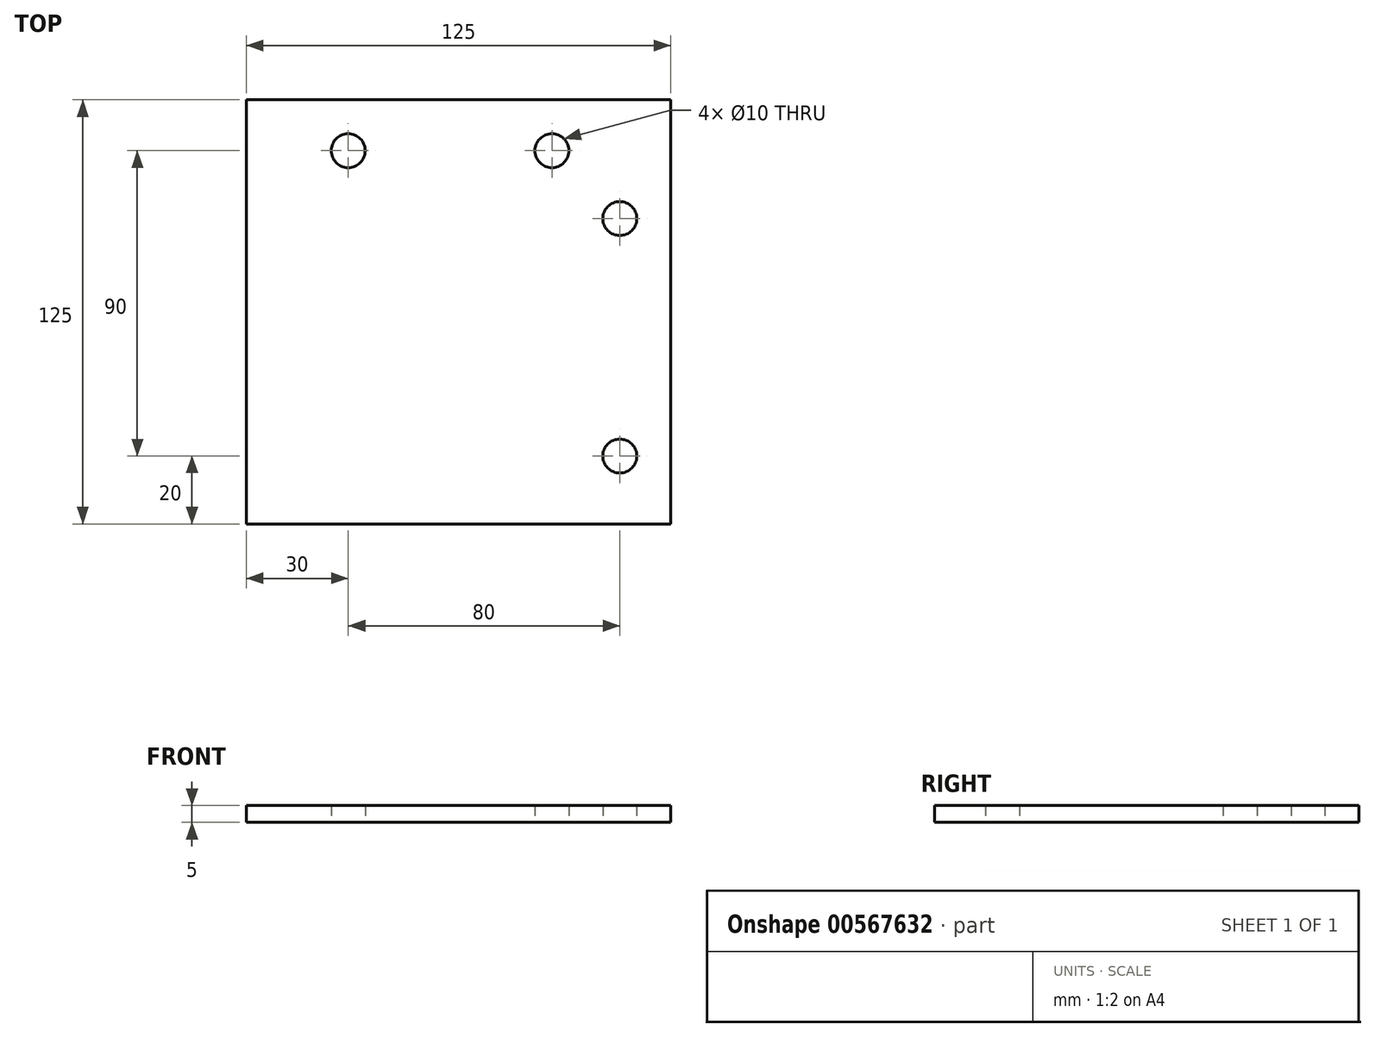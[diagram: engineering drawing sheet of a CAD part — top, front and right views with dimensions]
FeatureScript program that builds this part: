
annotation { "Feature Type Name" : "Feature", "Feature Type Description" : "" }
export const myFeature = defineFeature(function(context is Context, id is Id, definition is map)
    precondition{}
    {
        {
            var Q0;
            Q0=qCreatedBy(makeId("Top.planeOp"),FACE);
            var sketch = newSketch(context, id + "F0", { "sketchPlane" : qUnion([Q0])});
            skLineSegment(sketch, "E0.bottom", {"start": v(62.5, -62.5) * mm, "end": v(-62.5, -62.5) * mm});
            skLineSegment(sketch, "E0.top", {"start": v(62.5, 62.5) * mm, "end": v(-62.5, 62.5) * mm});
            skLineSegment(sketch, "E0.left", {"start": v(62.5, -62.5) * mm, "end": v(62.5, 62.5) * mm});
            skLineSegment(sketch, "E0.right", {"start": v(-62.5, -62.5) * mm, "end": v(-62.5, 62.5) * mm});
            skPoint(sketch, "E0.middle", {"position": v(0, 0) * mm});
            skCircle(sketch, "E1", {"center": v(27.5, 47.5) * mm, "radius": 5 * mm});
            skCircle(sketch, "E2", {"center": v(-32.5, 47.5) * mm, "radius": 5 * mm});
            skCircle(sketch, "E3", {"center": v(47.5, 27.5) * mm, "radius": 5 * mm});
            skCircle(sketch, "E4", {"center": v(47.5, -42.5) * mm, "radius": 5 * mm});
            skSolve(sketch);
        }
        {
            var Q0;
            Q0=makeQuery(id+"F0.imprint","IMPRINT",FACE,{"disambiguationData":[TD([[makeQuery(id+"F0.imprint","IMPRINT",EDGE,{"derivedFrom":sQuery(id+"F0.wireOp",EDGE,"E0.bottom")}),-1.0]])]});
            extrude(context, id + "F1", {"entities" : qUnion([Q0]), "depth" : 5 * mm, "offsetDistance" : 25 * mm});
        }
    });
